# Revit family: 50665 Varionaut 150
name_source: partatom
category: Körper
revit_build: Autodesk Revit 2015 (Build: 20140606_1530(x64)
units: mm (PartAtom-declared; Revit-internal decimal feet)

## types (1)
- 50665_Varionaut 150/24V/DMX/02
    Beschreibung = controllable pumps
    Dimensionsincl incl. filter LxWxH = 311x161x158
    Dynamic behaviour speed/ time to reach full fountain height from 0 - 100% with comet 5-8 = 1 s
    Environmental conditions, dry application = Ambient temperature max. 30°C with natural convection, max 40°C with forced convection, no direct sun exposure permitted
    Environmental conditions, submersible application = Water temperature min. 4°C to max. 35°C
    Filter housing = Plastic / stainless steel 1.4301 (AISI 304)
    Filter surface = 220 cm²
    H max = 5 m
    Hersteller = OASE GmbH Post Box 2069, 48469 Hörstel , Germany +49 5454 80-0
    Homepage = http://www.oase-livingwater.com
    Immersion depth max. = 4 m
    Input DMX = 1 m BUS cable with DMX box
    Input power = 1 m 24 V power cable with power box
    Max. powering up / min. Off time = 1 x per minute / 10 s
    Modell = Varionaut 150/24V/DMX/02
    MotorType / Electronic = 24 V DC EC-Motor, DMX controlled (DMX-RDM enabled)
    Name = Varionaut 150/24V/DMX/02
    Norminal voltage = 24 V/DC
    Number of BMX chanels = 2 channels (control channel, speed channel)
    Pressure side connection = 1 1/2  inch
    Protection class = IP 68
    Pump housing = Plastic
    Q max = 145 l/min
    Qmin Offset-Modus - DMX 0 = 22 l/min
    Suction side connection = 1 1/2  inch
    Weight = 5 kg
    oder no. = 50665
    power max. = 120 W

## geometry (parser evidence)
native form markers: Blend x6
no freeform markers — native parametric forms only
